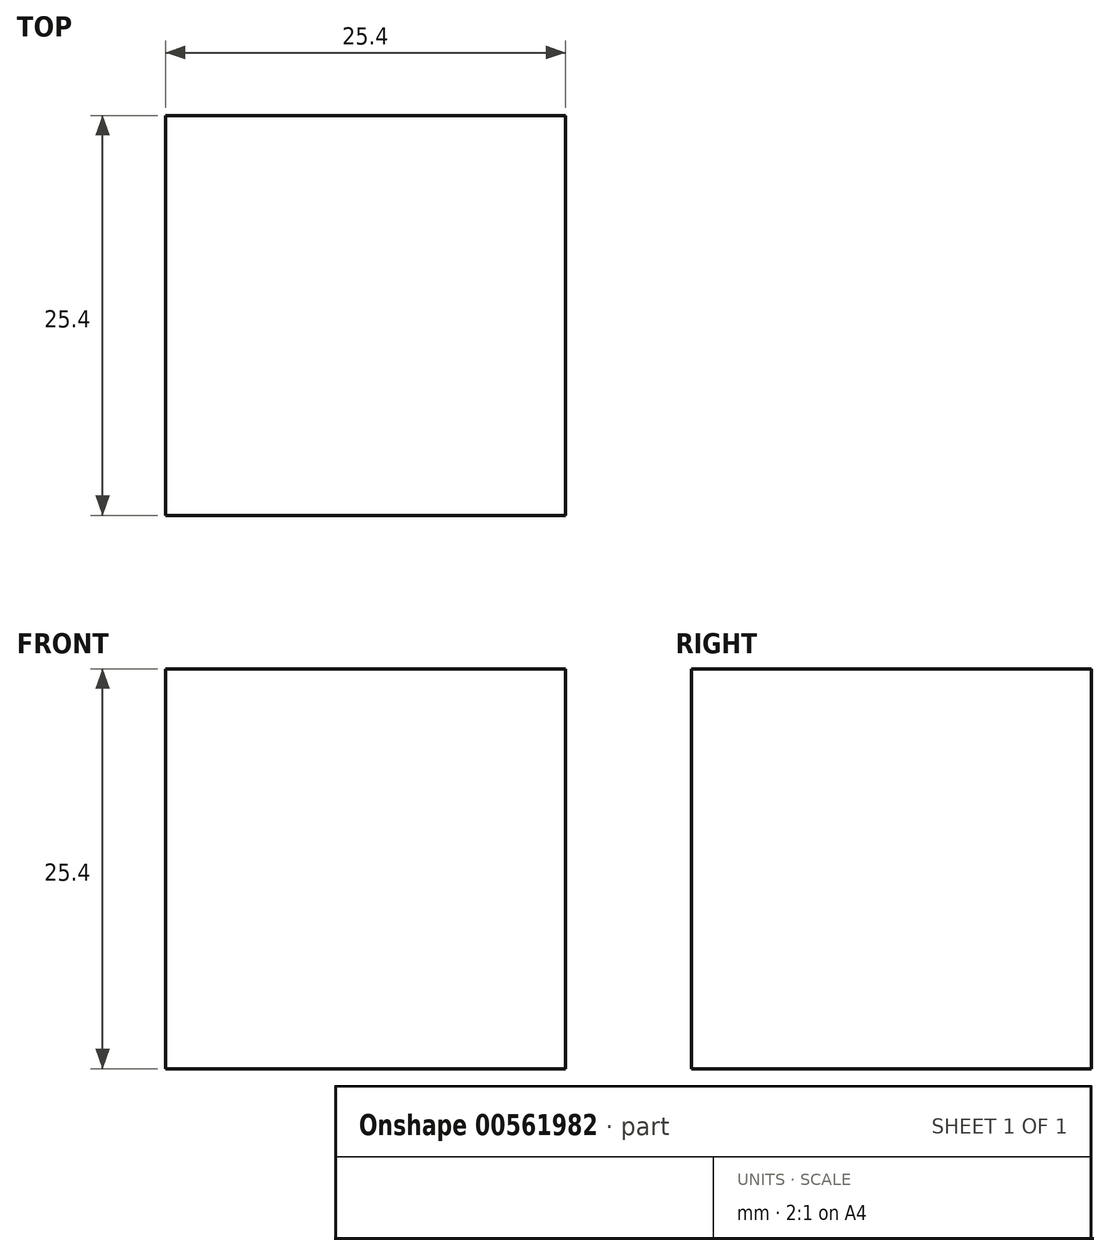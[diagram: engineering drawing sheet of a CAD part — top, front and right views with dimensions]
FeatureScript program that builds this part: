
annotation { "Feature Type Name" : "Feature", "Feature Type Description" : "" }
export const myFeature = defineFeature(function(context is Context, id is Id, definition is map)
    precondition{}
    {
        {
            var Q0;
            Q0=qCreatedBy(makeId("Front.planeOp"),FACE);
            var sketch = newSketch(context, id + "F0", { "sketchPlane" : qUnion([Q0])});
            skLineSegment(sketch, "E0.bottom", {"start": v(-25.4, 38.16) * mm, "end": v(0, 38.16) * mm});
            skLineSegment(sketch, "E0.top", {"start": v(-25.4, 12.76) * mm, "end": v(0, 12.76) * mm});
            skLineSegment(sketch, "E0.left", {"start": v(-25.4, 38.16) * mm, "end": v(-25.4, 12.76) * mm});
            skLineSegment(sketch, "E0.right", {"start": v(0, 38.16) * mm, "end": v(0, 12.76) * mm});
            skSolve(sketch);
        }
        {
            var Q0;
            Q0=makeQuery(id+"F0.imprint","IMPRINT",FACE,{"disambiguationData":[TD([[makeQuery(id+"F0.imprint","IMPRINT",EDGE,{"derivedFrom":sQuery(id+"F0.wireOp",EDGE,"E0.bottom")}),-1.0]])]});
            extrude(context, id + "F1", {"entities" : qUnion([Q0]), "depth" : 25.4 * mm, "offsetDistance" : 25.4 * mm});
        }
    });
